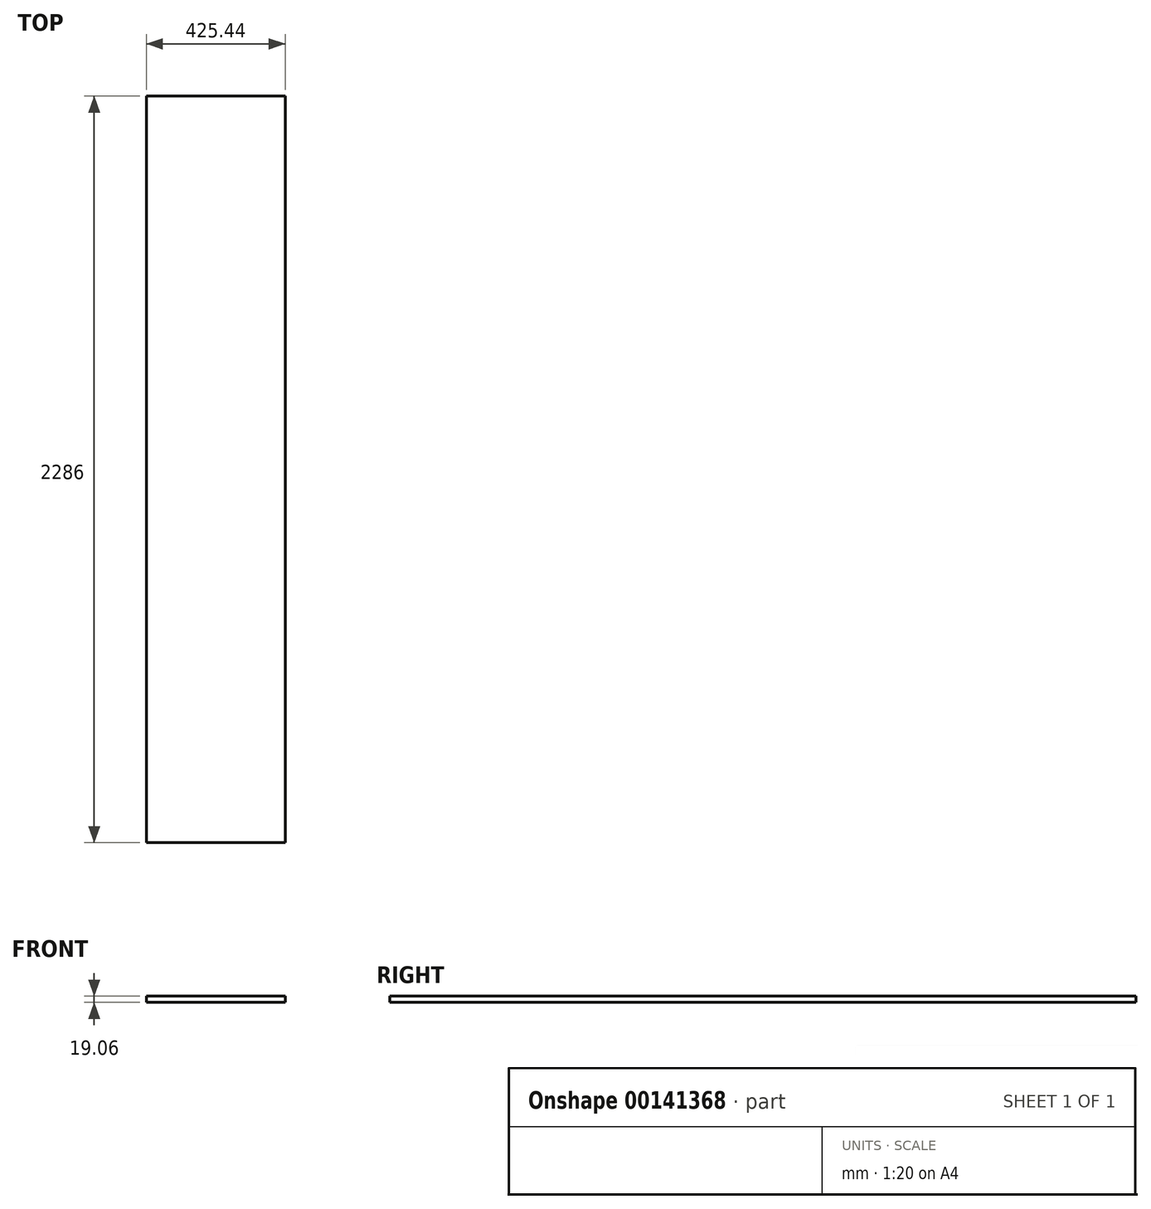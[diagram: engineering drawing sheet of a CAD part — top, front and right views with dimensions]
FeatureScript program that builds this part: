
annotation { "Feature Type Name" : "Feature", "Feature Type Description" : "" }
export const myFeature = defineFeature(function(context is Context, id is Id, definition is map)
    precondition{}
    {
        {
            var Q0;
            Q0=qCreatedBy(makeId("Front.planeOp"),FACE);
            var sketch = newSketch(context, id + "F0", { "sketchPlane" : qUnion([Q0])});
            skLineSegment(sketch, "E0.bottom", {"start": v(-212.73, 9.53) * mm, "end": v(212.72, 9.53) * mm});
            skLineSegment(sketch, "E0.top", {"start": v(-212.72, -9.53) * mm, "end": v(212.72, -9.53) * mm});
            skLineSegment(sketch, "E0.left", {"start": v(-212.73, 9.53) * mm, "end": v(-212.73, -9.52) * mm});
            skLineSegment(sketch, "E0.right", {"start": v(212.72, 9.53) * mm, "end": v(212.72, -9.52) * mm});
            skPoint(sketch, "E0.middle", {"position": v(0, 0) * mm});
            skSolve(sketch);
        }
        {
            var Q0;
            Q0 = qSketchRegion(id + "F0", true);
            extrude(context, id + "F1", {"entities" : qUnion([Q0]), "depth" : 2286 * mm});
        }
    });
